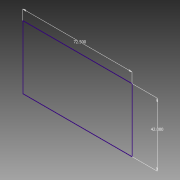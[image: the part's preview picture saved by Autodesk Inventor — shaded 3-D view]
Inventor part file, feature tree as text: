
AUTODESK INVENTOR PART (.ipt)
format: ipt  version: 2013 (Build 170138000, 138)  size: 60,928 bytes
history: native  units: in
note: dims shown in document units (in); Inventor stores cm internally (conversion verified against a paired STEP export)
features: sketch x1
ambient origin geometry x8: Origin, YZ Plane, XZ Plane, XY Plane, X Axis, Y Axis, Z Axis, Center Point
feature tree (1):
  sketch  "Sketch1"  dims[d0=72.5in d1=42.0in]
